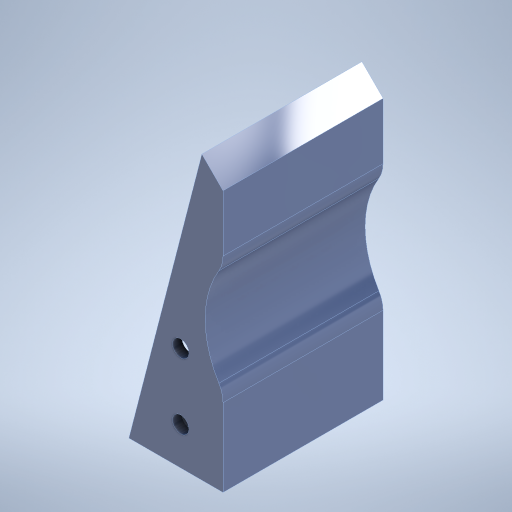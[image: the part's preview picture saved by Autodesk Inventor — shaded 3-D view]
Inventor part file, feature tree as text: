
AUTODESK INVENTOR PART (.ipt)
format: ipt  version: 2024.2 (Build 282272000, 272)  size: 300,032 bytes
history: native  units: mm
features: extrude x6, sketch x6, chamfer x1, fillet x1, shell x1
ambient origin geometry x8: Origin, YZ Plane, XZ Plane, XY Plane, X Axis, Y Axis, Z Axis, Center Point
bodies: Solid1 (feature_tree)
feature tree (15):
  extrude  "Extrusion1"  Depth=20.0mm
  chamfer  "Chamfer1"  Distance=60.0mm
  extrude  "Extrusion2"  Depth=2.0mm TaperAngle=0.0deg
  extrude  "Extrusion3"  Depth=2.0mm TaperAngle=0.0deg
  fillet  "Fillet1"  Radius=6.0mm
  shell  "Shell1"  Thickness=2.0mm
  extrude  "Extrusion4"  Depth=30.0mm
  extrude  "Extrusion5"  Depth=34.0mm TaperAngle=0.0deg
  extrude  "Extrusion6"  Depth=10.0mm
  sketch  "Sketch1"  dims[d0=34.0mm d1=20.0mm d2=60.0mm d3=0.0mm]
  sketch  "Sketch3"  dims[d4=4.5mm d5=2.0mm d6=45.0deg d7=60.0mm d8=0.0mm]
  sketch  "Sketch4"  dims[d9=39.6mm d10=60.0mm d11=0.0mm d12=6.0mm d13=2.0mm]
  sketch  "Sketch5"  dims[d14=16.0mm d15=30.0mm]
  sketch  "Sketch6"  dims[d16=3.0mm d17=34.0mm d18=0.0mm]
  sketch  "Sketch7"  dims[d19=4.5mm d20=4.5mm d21=5.0mm d22=20.0mm d24=10.0mm d25=20.0mm d27=25.0mm d30=3.0mm d31=0.0mm d32=3.5mm d33=8.0mm d34=11.0mm d35=20.0mm d37=14.0mm d38=10.0mm d40=10.0mm d42=0.0mm d43=0.0mm]
